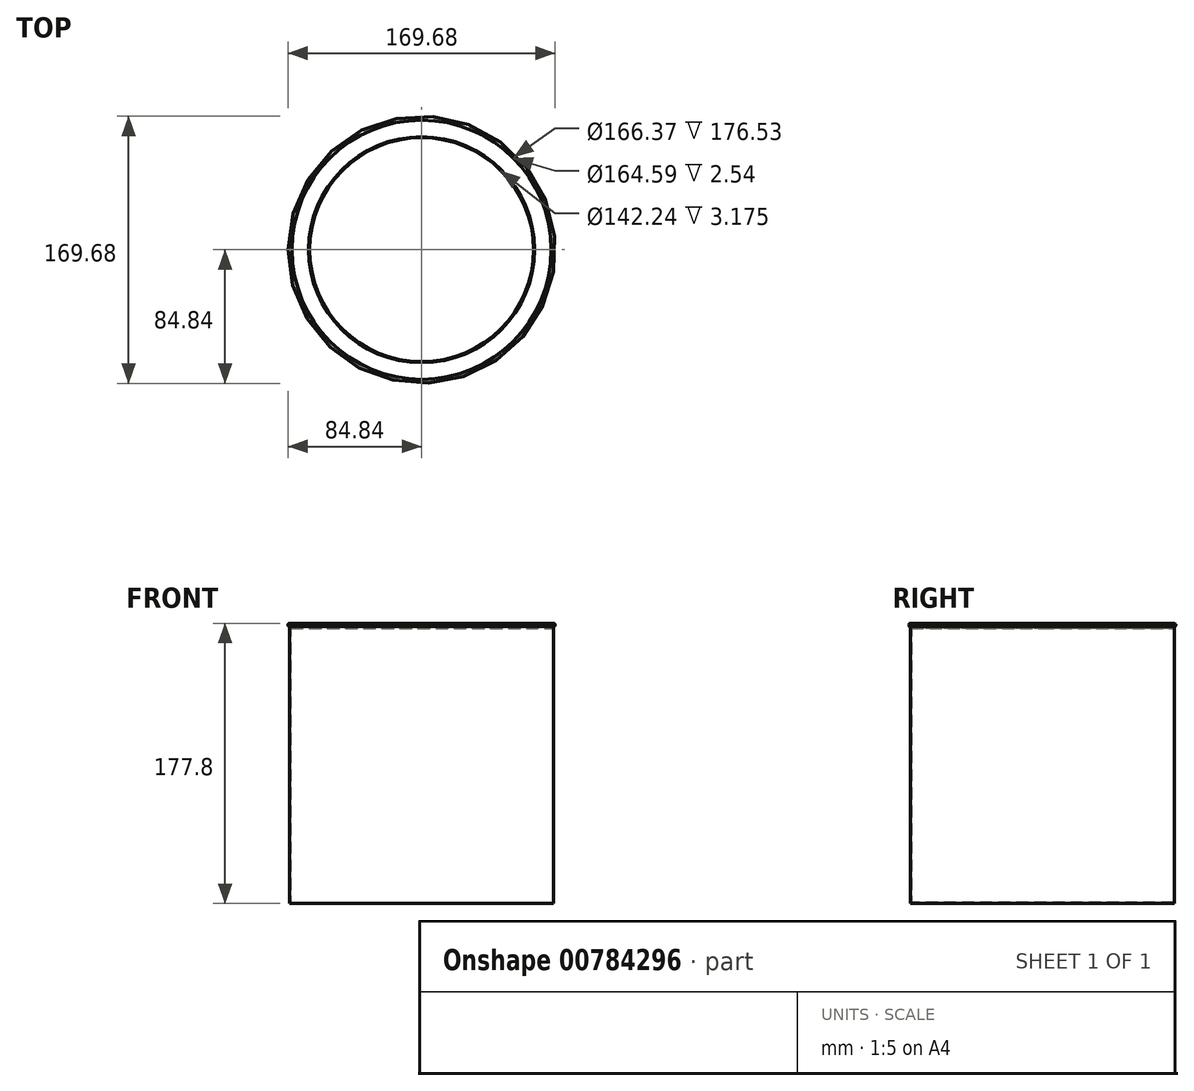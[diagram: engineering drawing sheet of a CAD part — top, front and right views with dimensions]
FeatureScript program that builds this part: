
annotation { "Feature Type Name" : "Feature", "Feature Type Description" : "" }
export const myFeature = defineFeature(function(context is Context, id is Id, definition is map)
    precondition{}
    {
        {
            var Q0;
            Q0=qCreatedBy(makeId("Right.planeOp"),FACE);
            var sketch = newSketch(context, id + "F0", { "sketchPlane" : qUnion([Q0])});
            skLineSegment(sketch, "E0", {"start": v(0, 0) * mm, "end": v(0, 96.46) * mm, "construction": true});
            skLineSegment(sketch, "E1", {"start": v(0, 0) * mm, "end": v(83.82, 0) * mm});
            skLineSegment(sketch, "E2", {"start": v(83.82, 0) * mm, "end": v(83.82, 175.77) * mm});
            skArc(sketch, "E3", {"start": v(83.82, 175.77) * mm, "mid": v(84.84, 176.78) * mm, "end": v(83.82, 177.8) * mm});
            skLineSegment(sketch, "E4", {"start": v(83.82, 177.8) * mm, "end": v(82.3, 177.8) * mm});
            skLineSegment(sketch, "E5", {"start": v(82.3, 177.8) * mm, "end": v(82.3, 175.26) * mm});
            skLineSegment(sketch, "E6", {"start": v(82.3, 175.26) * mm, "end": v(71.75, 175.26) * mm});
            skLineSegment(sketch, "E7", {"start": v(71.75, 175.26) * mm, "end": v(71.75, 177.8) * mm});
            skLineSegment(sketch, "E8", {"start": v(71.75, 177.8) * mm, "end": v(71.12, 177.8) * mm});
            skLineSegment(sketch, "E9", {"start": v(71.12, 177.8) * mm, "end": v(71.12, 174.62) * mm});
            skLineSegment(sketch, "E10", {"start": v(82.93, 177.17) * mm, "end": v(83.18, 177.17) * mm});
            skLineSegment(sketch, "E11", {"start": v(83.18, 177.17) * mm, "end": v(83.19, 0.64) * mm});
            skLineSegment(sketch, "E12", {"start": v(83.19, 0.64) * mm, "end": v(0, 0.63) * mm});
            skLineSegment(sketch, "E13", {"start": v(0, 0.63) * mm, "end": v(0, 0) * mm});
            skLineSegment(sketch, "E14", {"start": v(82.93, 177.17) * mm, "end": v(82.93, 174.62) * mm});
            skLineSegment(sketch, "E15", {"start": v(82.93, 174.62) * mm, "end": v(71.12, 174.62) * mm});
            skSolve(sketch);
        }
        {
            var Q0;
            Q0=makeQuery(id+"F0.imprint","IMPRINT",FACE,{"disambiguationData":[TD([[makeQuery(id+"F0.imprint","IMPRINT",EDGE,{"derivedFrom":sQuery(id+"F0.wireOp",EDGE,"E1")}),1.0]])]});
            var Q1;
            Q1=sQuery(id+"F0.wireOp",EDGE,"E0");
            revolve(context, id + "F1", {"surfaceOperationType" : NewSurfaceOperationType.NEW, "entities" : qUnion([Q0]), "axis" : qUnion([Q1]), "revolveType" : RevolveType.FULL});
        }
    });
